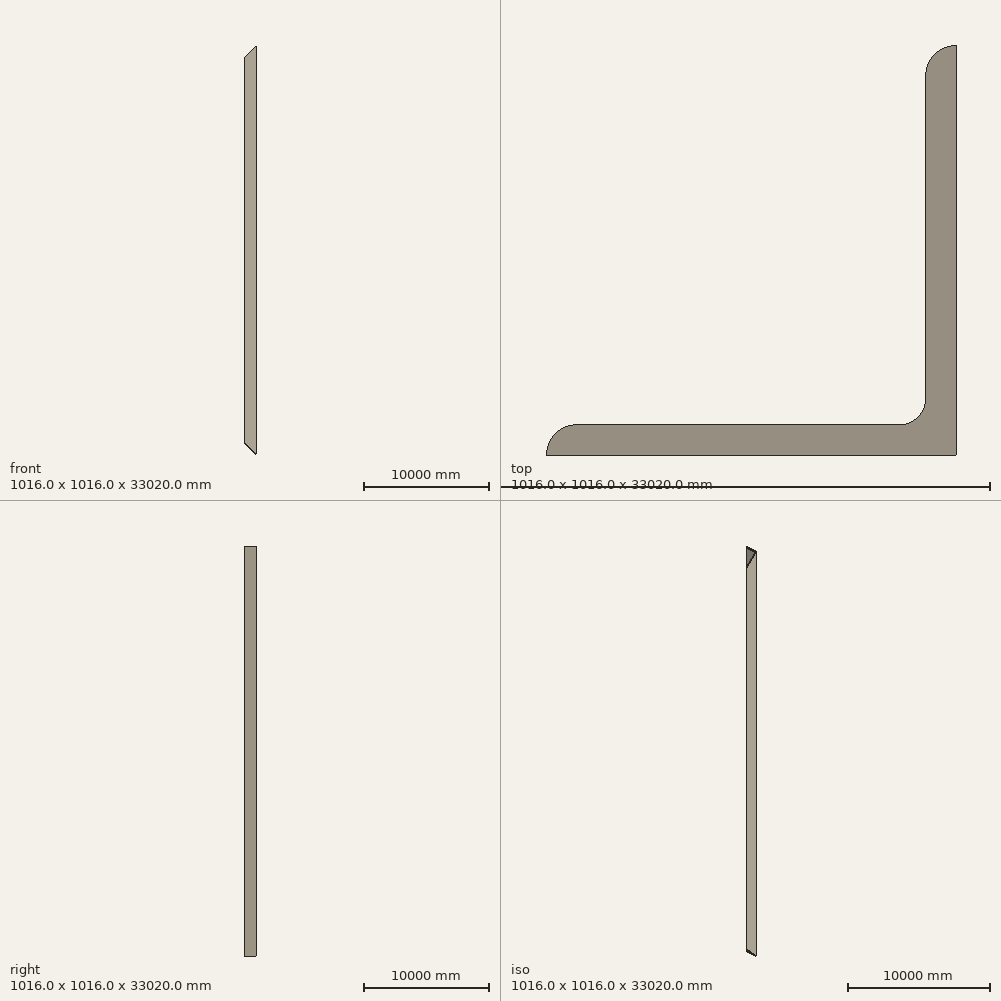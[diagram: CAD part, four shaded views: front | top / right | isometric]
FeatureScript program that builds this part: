
annotation { "Feature Type Name" : "Feature", "Feature Type Description" : "" }
export const myFeature = defineFeature(function(context is Context, id is Id, definition is map)
    precondition{}
    {
        {
            var Q0;
            Q0=qCreatedBy(makeId("Top.planeOp"),FACE);
            var sketch = newSketch(context, id + "F0", { "sketchPlane" : qUnion([Q0])});
            skLineSegment(sketch, "E0", {"start": v(0, 0) * mm, "end": v(1016, 0) * mm});
            skLineSegment(sketch, "E1", {"start": v(1016, 0) * mm, "end": v(1016, 1016) * mm});
            skLineSegment(sketch, "E2", {"start": v(939.8, 939.8) * mm, "end": v(939.8, 139.7) * mm});
            skLineSegment(sketch, "E3", {"start": v(876.3, 76.2) * mm, "end": v(76.2, 76.2) * mm});
            skArc(sketch, "E4", {"start": v(0, 0) * mm, "mid": v(22.32, 53.88) * mm, "end": v(76.2, 76.2) * mm});
            skArc(sketch, "E5", {"start": v(939.8, 939.8) * mm, "mid": v(962.12, 993.68) * mm, "end": v(1016, 1016) * mm});
            skPoint(sketch, "E6.visualSharp", {"position": v(939.8, 76.2) * mm});
            skArc(sketch, "E6.filletArc", {"start": v(876.3, 76.2) * mm, "mid": v(921.2, 94.8) * mm, "end": v(939.8, 139.7) * mm});
            skSolve(sketch);
        }
        {
            var Q0;
            Q0 = qSketchRegion(id + "F0", true);
            extrude(context, id + "F1", {"entities" : qUnion([Q0]), "depth" : 33020 * mm, "offsetDistance" : 25.4 * mm});
        }
        {
            var Q0;
            Q0=makeQuery(id+"F1.opExtrude","SWEPT_FACE",FACE,{"disambiguationData":[OSD([sQuery(id+"F0.wireOp",EDGE,"E0")])]});
            var sketch = newSketch(context, id + "F2", { "sketchPlane" : qUnion([Q0])});
            skLineSegment(sketch, "E7", {"start": v(1016, 33020) * mm, "end": v(-182.12, 31821.88) * mm});
            skLineSegment(sketch, "E8", {"start": v(-182.12, 31821.88) * mm, "end": v(-491.9, 34519.5) * mm});
            skLineSegment(sketch, "E9", {"start": v(-491.9, 34519.5) * mm, "end": v(1016, 33020) * mm});
            skLineSegment(sketch, "E10", {"start": v(1016, 0) * mm, "end": v(-632.62, 1648.62) * mm});
            skLineSegment(sketch, "E11", {"start": v(-632.62, 1648.62) * mm, "end": v(-458.96, -1520.65) * mm});
            skLineSegment(sketch, "E12", {"start": v(-458.96, -1520.65) * mm, "end": v(1016, 0) * mm});
            skSolve(sketch);
        }
        {
            var Q0;
            {var subQ2=sQuery(id+"F2.wireOp",EDGE,"E8");Q0=makeQuery(id+"F2.imprint","IMPRINT",FACE,{"disambiguationData":[TD([[makeQuery(id+"F2.imprint","IMPRINT",EDGE,{"derivedFrom":subQ2}),-1.0]])]});}
            var Q1;
            {var subQ2=sQuery(id+"F2.wireOp",EDGE,"E11");Q1=makeQuery(id+"F2.imprint","IMPRINT",FACE,{"disambiguationData":[TD([[makeQuery(id+"F2.imprint","IMPRINT",EDGE,{"derivedFrom":subQ2}),1.0]])]});}
            var Q2;
            {var subQ1=sQuery(id+"F0.wireOp",EDGE,"E0");var subQ2=makeQuery(id+"F1.opExtrude","CAP_EDGE",EDGE,{"disambiguationData":[OSD([subQ1])],"isStart":true});Q2=makeQuery(id+"F2.imprint","IMPRINT",FACE,{"disambiguationData":[TD([[makeQuery(id+"F2.imprint","IMPRINT",EDGE,{"derivedFrom":subQ2}),1.0]])]});}
            var Q3;
            {var subQ1=sQuery(id+"F0.wireOp",EDGE,"E0");var subQ2=makeQuery(id+"F1.opExtrude","CAP_EDGE",EDGE,{"disambiguationData":[OSD([subQ1])],"isStart":false});Q3=makeQuery(id+"F2.imprint","IMPRINT",FACE,{"disambiguationData":[TD([[makeQuery(id+"F2.imprint","IMPRINT",EDGE,{"derivedFrom":subQ2}),-1.0]])]});}
            extrude(context, id + "F3", {"entities" : qUnion([Q0, Q1, Q2, Q3]), "operationType" : NewBodyOperationType.REMOVE, "endBound" : BoundingType.THROUGH_ALL, "oppositeDirection" : true, "depth" : 25.4 * mm, "offsetDistance" : 25.4 * mm});
        }
    });
